# Revit family: Grinder_Pump-Solid_Handling-Zoeller-71_Horizontal_Reversing_Series
name_source: partatom
category: Mechanical Equipment
units: mm (PartAtom-declared; Revit-internal decimal feet)

## family parameters
Always vertical = No
Cut with Voids When Loaded = No
OmniClass Number = 23.60.30.21
OmniClass Title = Pumps
Part Type = Normal
Room Calculation Point = No
Round Connector Dimension = Use Radius
Shared = Yes
Work Plane-Based = Yes

## types (9) — shared parameters
3" Discharge Size (Optional) = No
Assembly Code = D2010900
Default Elevation = 0"
Description = Horizontal Reversing Discharge. Commercial Grinder Pumps
Discharge Diameter = 2 1/2"
Discharge Radius = 1 1/4"
Height = 28 1/4"
Hertz = 60
Impeller Type = Bronze Vortex
Installation Type = Floor Mounted
Insulation = Class F
Lead Wires Insulation = Class F
Length = 13 13/16"
Manufacturer = Zoeller
Masterformat Number = 43 26 13
Masterformat Title = Submersible Grinder Pumps
Material = Cast Iron-Zoeller-Powder Coated Epoxy
Max. Stator Temp. = 311 °F
Max. Water Temp. = 104 °F
Moisture Detection = Moisture Sensing Probes (Requires a circuit in control panel to function)
Motor Shaft = 416 S.S.
Motor Thermal Shutoff = Thermal Sensors with Automatic Reset (Requires a circuit in control panel to function)
Motor Type = Submersible
Omniclass Table 23 Code = 23.60.30.21
Omniclass Table 23 Title = Pumps
Operation = Non-Automatic
Phase = 3
Power Cord = #12-4 SO (Models with a FLA greater than 20 amps use #8-4 gauge power cord)
Price = Prices may vary. Please consult Manufacturer Representative for most up-to-date price list.
Product Page URL = http://www.zoellerengprod.com
RPM = 3450
Revised Date = 04/24/2024
Service Factor = 1.2
Shaft Seal Lower (Options) = Carbon/Silicon Carbide, Silicon Carbide/Silicon Carbide
Shaft Seal Lower Standard = Carbon/Ceramic
Shaft Seal Upper (Options) = Carbon/Silicon Carbide Silicon Carbide/Silicon Carbide
Shaft Seal Upper Standard = Carbon/Ceramic
Shipping Weight = 245 lbs (111 kg)
Tandem Seals = Standard
Type = 3 Phase
Type SOW Power Cord Length = 300"
URL = http://www.zoellerengprod.com
Warranty Information = 36 Months (Limited)
Waste Connection = Yes
Width = 11 3/4"

## per-type parameters (varying)
| type | Apparent Load | Flow @ 4' | Full Load Amps | Locked Rotor Amps | Maximum KW Input | Model | Motor | Motor Design Letter | NEC Locked Rotor Code | Voltage |
| 7110 - 2.5" - 3" 208V 3Ph | 3598 VA | 89 GPM | 17 A | 66 A | 5.3 | 7110-2 1/2"-3" | 3.0 BHP | NEMA B (3 Ph), NEMA L (1 Ph) | M (1 Ph), G (3 Ph) | 208 V |
| 7110 - 2.5" - 3" 230V 3Ph | 3473 VA | 89 GPM | 15 A | 57 A | 5.3 | 7110-2 1/2"-3" | 3.0 BHP | NEMA B (3 Ph), NEMA L (1 Ph) | M (1 Ph), G (3 Ph) | 230 V |
| 7110 - 2.5" - 3" 460V 3Ph | 3450 VA | 89 GPM | 8 A | 29 A | 5.3 | 7110-2 1/2"-3" | 3.0 BHP | NEMA B (3 Ph), NEMA L (1 Ph) | M (1 Ph), G (3 Ph) | 460 V |
| 7111 - 2.5" - 3" 208V 3Ph | 4306 VA | 94 GPM | 21 A | 94 A | 6.4 | 7111-2 1/2"-3" | 5.0 BHP | NEMA B (3 Ph), NEMA L (1 Ph) | G (1 Ph), H (3 Ph) | 208 V |
| 7111 - 2.5" - 3" 230V 3Ph | 4140 VA | 94 GPM | 18 A | 82 A | 6.4 | 7111-2 1/2"-3" | 5.0 BHP | NEMA B (3 Ph), NEMA L (1 Ph) | G (1 Ph), H (3 Ph) | 230 V |
| 7111 - 2.5" - 3" 460V 3Ph | 4140 VA | 94 GPM | 9 A | 41 A | 6.4 | 7111-2 1/2"-3" | 5.0 BHP | NEMA B (3 Ph), NEMA L (1 Ph) | G (1 Ph), H (3 Ph) | 460 V |
| 7112 - 2.5" - 3" 208V 3Ph | 5262 VA | 94 GPM | 25 A | 94 A | 8.0 | 7112-2 1/2"-3" | 7.5 BHP | NEMA B (3 Ph) | D | 208 V |
| 7112 - 2.5" - 3" 230V 3Ph | 5060 VA | 94 GPM | 22 A | 82 A | 8.0 | 7112-2 1/2"-3" | 7.5 BHP | NEMA B (3 Ph) | D | 230 V |
| 7112 - 2.5" - 3" 460V 3Ph | 5060 VA | 94 GPM | 11 A | 41 A | 8.0 | 7112-2 1/2"-3" | 7.5 BHP | NEMA B (3 Ph) | D | 460 V |

## geometry (parser evidence)
native form markers: Sweep x2
no freeform markers — native parametric forms only
